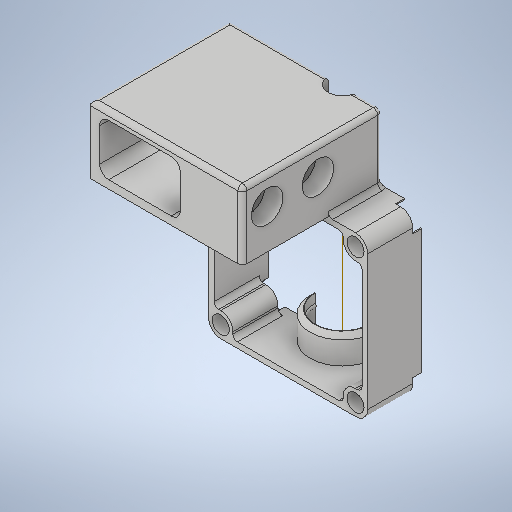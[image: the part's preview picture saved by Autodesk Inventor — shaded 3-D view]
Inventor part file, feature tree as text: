
AUTODESK INVENTOR PART (.ipt)
format: ipt  version: 2025 (Build 290162000, 162)  size: 662,528 bytes
history: native  units: mm
features: extrude x17, fillet x4, pattern_circular x3, mirror x2, sketch x2, other x1, revolve x1, chamfer x1
ambient origin geometry x8: Origin, YZ Plane, XZ Plane, XY Plane, X Axis, Y Axis, Z Axis, Center Point
bodies: Volumenkörper1 (feature_tree)
feature tree (31):
  extrude  "Extrusion1"  Depth=35.3mm
  extrude  "Extrusion2"  Depth=10.0mm
  extrude  "Extrusion3"  Depth=10.0mm TaperAngle=0.0deg
  extrude  "Extrusion4"  Depth=10.0mm
  extrude  "Extrusion5"  Depth=10.0mm
  pattern_circular  "Runde Anordnung1"  [2 undecoded]
  pattern_circular  "Runde Anordnung2"  [2 undecoded]
  fillet  "Rundung1"  Radius=3.8mm
  extrude  "Extrusion6"  Depth=10.0mm TaperAngle=0.0deg
  extrude  "Extrusion7"  Depth=10.0mm
  mirror  "Spiegeln1"
  other  "Arbeitsachse1"
  revolve  "Umdrehung1"
  mirror  "Spiegeln2"
  fillet  "Rundung2"  Radius=12.0mm
  chamfer  "Fase1"  Distance=1.45mm
  extrude  "Extrusion8"  Depth=10.0mm TaperAngle=0.0deg
  extrude  "Extrusion9"  Depth=10.0mm TaperAngle=360.0deg
  pattern_circular  "Runde Anordnung3"  Count=4 Angle=360.0deg
  fillet  "Rundung3"  Radius=2.7mm
  extrude  "Extrusion10"  Depth=10.0mm
  extrude  "Extrusion11"  Depth=10.0mm
  extrude  "Extrusion12"  Depth=10.0mm TaperAngle=0.0deg
  extrude  "Extrusion13"  Depth=10.0mm
  extrude  "Extrusion14"  Depth=10.0mm TaperAngle=0.0deg
  extrude  "Extrusion15"  Depth=10.0mm
  fillet  "Rundung4"  Radius=0.8mm
  extrude  "Extrusion17"  Depth=10.0mm
  extrude  "Extrusion18"  TaperAngle=180.0deg  [1 undecoded]
  sketch  "Skizze22"  dims[d0=35.3mm d1=35.3mm]
  sketch  "Skizze23"  dims[d2=32.8mm d3=32.8mm d4=12.0mm d5=0.0mm d6=5.4mm d7=3.8mm d9=1.45mm d10=12.0mm d11=0.0mm d12=3.8mm d13=12.0mm d14=0.0mm d15=1.45mm d16=12.0mm d17=0.0mm d18=1.45mm d19=12.0mm d20=0.0mm d21=40.0mm d22=360.0deg d24=40.0mm d25=360.0deg d27=2.7mm d28=12.0mm d29=17.65mm d30=12.0mm d31=0.0mm d32=14.2mm d33=6.0mm d34=0.0mm d35=0.25mm d36=0.8mm d37=4.5mm d38=180.0deg d39=0.45mm d40=1.0mm d41=2.0mm d42=45.0deg d43=5.4mm d44=2.0mm d45=0.0mm d46=0.253064mm d47=0.151856mm d48=0.263167mm d49=0.252607mm d51=2.0mm d52=0.0mm d53=40.0mm d54=360.0deg d56=1.0mm d57=33.75mm d58=15.0mm d62=31.0mm d63=0.0mm d64=6.2mm d65=12.0mm d66=0.0mm d67=2.0mm d68=0.0mm d69=3.0mm d70=7.0mm d71=5.25mm d72=3.1mm d73=29.0mm d74=0.0mm d75=7.0mm d76=4.1mm d77=4.0mm d78=0.0mm d79=4.1mm d80=15.5mm d81=0.0mm d84=25.5mm d88=1.0mm d90=15.0mm d91=17.9mm d92=2.0mm d93=1.8mm d94=7.0mm d95=4.0mm d96=0.0mm d97=4.1mm d98=10.0mm d99=0.0mm d103=2.1mm d104=11.4mm d105=7.25mm]
note: 5 required parameter values undecoded (feature->parameter linkage not recoverable at this tier; creation-order binding heuristic only, values carry confidence <= 0.55)
